FCSTD DOCUMENT  (FreeCAD 0.18R14555 (Git shallow))
Label: t-slot-profile
License: All rights reserved
LicenseURL: http://en.wikipedia.org/wiki/All_rights_reserved
objects: Sketcher::SketchObject×1, PartDesign::Body×1
note: 2 computed .brp shape members not serialized (recipe doc carries the construction recipe); baked Part::Feature solids carry a one-line shape summary decoded from their .brp

FEATURE [Sketcher::SketchObject] Sketch
  MapMode = 5
  Support = -> [XY_Plane]
  sketch-geometry (30):
    g0: LineSegment StartX=-20 StartY=-20 StartZ=0 EndX=-20 EndY=-5 EndZ=0
    g1: LineSegment StartX=-20 StartY=-5 StartZ=0 EndX=-7.5 EndY=-5 EndZ=0
    g2: LineSegment StartX=-7.5 StartY=-5 StartZ=0 EndX=-7.5 EndY=5 EndZ=0
    g3: LineSegment StartX=-7.5 StartY=5 StartZ=0 EndX=-20 EndY=5 EndZ=0
    g4: LineSegment StartX=-20 StartY=5 StartZ=0 EndX=-20 EndY=20 EndZ=0
    g5: LineSegment StartX=-20 StartY=20 StartZ=0 EndX=-5 EndY=20 EndZ=0
    g6: LineSegment StartX=-5 StartY=20 StartZ=0 EndX=-5 EndY=7.5 EndZ=0
    g7: LineSegment StartX=-5 StartY=7.5 StartZ=0 EndX=5 EndY=7.5 EndZ=0
    g8: LineSegment StartX=5 StartY=7.5 StartZ=0 EndX=5 EndY=20 EndZ=0
    g9: LineSegment StartX=5 StartY=20 StartZ=0 EndX=20 EndY=20 EndZ=0
    g10: LineSegment StartX=20 StartY=20 StartZ=0 EndX=20 EndY=5 EndZ=0
    g11: LineSegment StartX=20 StartY=5 StartZ=0 EndX=7.5 EndY=5 EndZ=0
    g12: LineSegment StartX=7.5 StartY=5 StartZ=0 EndX=7.5 EndY=-5 EndZ=0
    g13: LineSegment StartX=7.5 StartY=-5 StartZ=0 EndX=20 EndY=-5 EndZ=0
    g14: LineSegment StartX=20 StartY=-5 StartZ=0 EndX=20 EndY=-20 EndZ=0
    g15: LineSegment StartX=20 StartY=-20 StartZ=0 EndX=5 EndY=-20 EndZ=0
    g16: LineSegment StartX=5 StartY=-20 StartZ=0 EndX=5 EndY=-7.5 EndZ=0
    g17: LineSegment StartX=5 StartY=-7.5 StartZ=0 EndX=-5 EndY=-7.5 EndZ=0
    g18: LineSegment StartX=-5 StartY=-7.5 StartZ=0 EndX=-5 EndY=-20 EndZ=0
    g19: LineSegment StartX=-5 StartY=-20 StartZ=0 EndX=-20 EndY=-20 EndZ=0
    g20: LineSegment [constr] StartX=-5 StartY=-7.5 StartZ=0 EndX=-5 EndY=7.5 EndZ=0
    g21: LineSegment [constr] StartX=5 StartY=7.5 StartZ=0 EndX=5 EndY=-7.5 EndZ=0
    g22: LineSegment [constr] StartX=-7.5 StartY=5 StartZ=0 EndX=7.5 EndY=5 EndZ=0
    g23: LineSegment [constr] StartX=7.5 StartY=-5 StartZ=0 EndX=-7.5 EndY=-5 EndZ=0
    g24: LineSegment [constr] StartX=-20 StartY=-5 StartZ=0 EndX=-20 EndY=5 EndZ=0
    g25: LineSegment [constr] StartX=-5 StartY=20 StartZ=0 EndX=5 EndY=20 EndZ=0
    g26: LineSegment [constr] StartX=20 StartY=5 StartZ=0 EndX=20 EndY=-5 EndZ=0
    g27: LineSegment [constr] StartX=-5 StartY=-20 StartZ=0 EndX=5 EndY=-20 EndZ=0
    g28: LineSegment [constr] StartX=20 StartY=-20 StartZ=0 EndX=-20 EndY=20 EndZ=0
    g29: LineSegment [constr] StartX=-20 StartY=-20 StartZ=0 EndX=20 EndY=20 EndZ=0
  constraints (80):
    c: Vertical(g0)
    c: Coincident(g0,g1)
    c: Horizontal(g1)
    c: Coincident(g1,g2)
    c: Vertical(g2)
    c: Coincident(g2,g3)
    c: Horizontal(g3)
    c: Coincident(g3,g4)
    c: Vertical(g4)
    c: Coincident(g4,g5)
    c: Horizontal(g5)
    c: Coincident(g5,g6)
    c: Vertical(g6)
    c: Coincident(g6,g7)
    c: Horizontal(g7)
    c: Coincident(g7,g8)
    c: Vertical(g8)
    c: Coincident(g8,g9)
    c: Horizontal(g9)
    c: Coincident(g9,g10)
    c: Vertical(g10)
    c: Coincident(g10,g11)
    c: Coincident(g11,g12)
    c: Coincident(g12,g13)
    c: Horizontal(g13)
    c: Coincident(g13,g14)
    c: Vertical(g14)
    c: Coincident(g14,g15)
    c: Horizontal(g15)
    c: Coincident(g15,g16)
    c: Vertical(g16)
    c: Coincident(g16,g17)
    c: Horizontal(g17)
    c: Coincident(g17,g18)
    c: Vertical(g18)
    c: Coincident(g18,g19)
    c: Coincident(g19,g0)
    c: Horizontal(g19)
    c: Horizontal(g11)
    c: Vertical(g12)
    c: Coincident(g20,g17)
    c: Coincident(g20,g6)
    c: Coincident(g21,g7)
    c: Coincident(g21,g16)
    c: Vertical(g21)
    c: Vertical(g20)
    c: Coincident(g22,g2)
    c: Coincident(g22,g11)
    c: Coincident(g23,g12)
    c: Coincident(g23,g1)
    c: Horizontal(g23)
    c: Horizontal(g22)
    c: Coincident(g24,g0)
    c: Coincident(g24,g3)
    c: Vertical(g24)
    c: Coincident(g25,g5)
    c: Coincident(g25,g8)
    c: Horizontal(g25)
    c: Coincident(g26,g10)
    c: Coincident(g26,g13)
    c: Vertical(g26)
    c: Coincident(g27,g18)
    c: Coincident(g27,g15)
    c: Horizontal(g27)
    c: Coincident(g28,g14)
    c: Coincident(g29,g0)
    c: Coincident(g29,g9)
    c: Coincident(g28,g4)
    c: Equal(g0,g19)
    c: Equal(g4,g5)
    c: Equal(g9,g10)
    c: Equal(g2,g7)
    c: Equal(g3,g6)
    c: Equal(g11,g3)
    c: Equal(g1,g18)
    c: DistanceY(g0,g4) = 40
    c: DistanceY(g2,g2) = 10
    c: DistanceY(g18,g18) = 12.5
    c: PointOnObject(g-1,g29)
    c: PointOnObject(g-1,g28)
FEATURE [PartDesign::Body] Body
  Group = -> [Sketch]
  Origin = -> Origin
